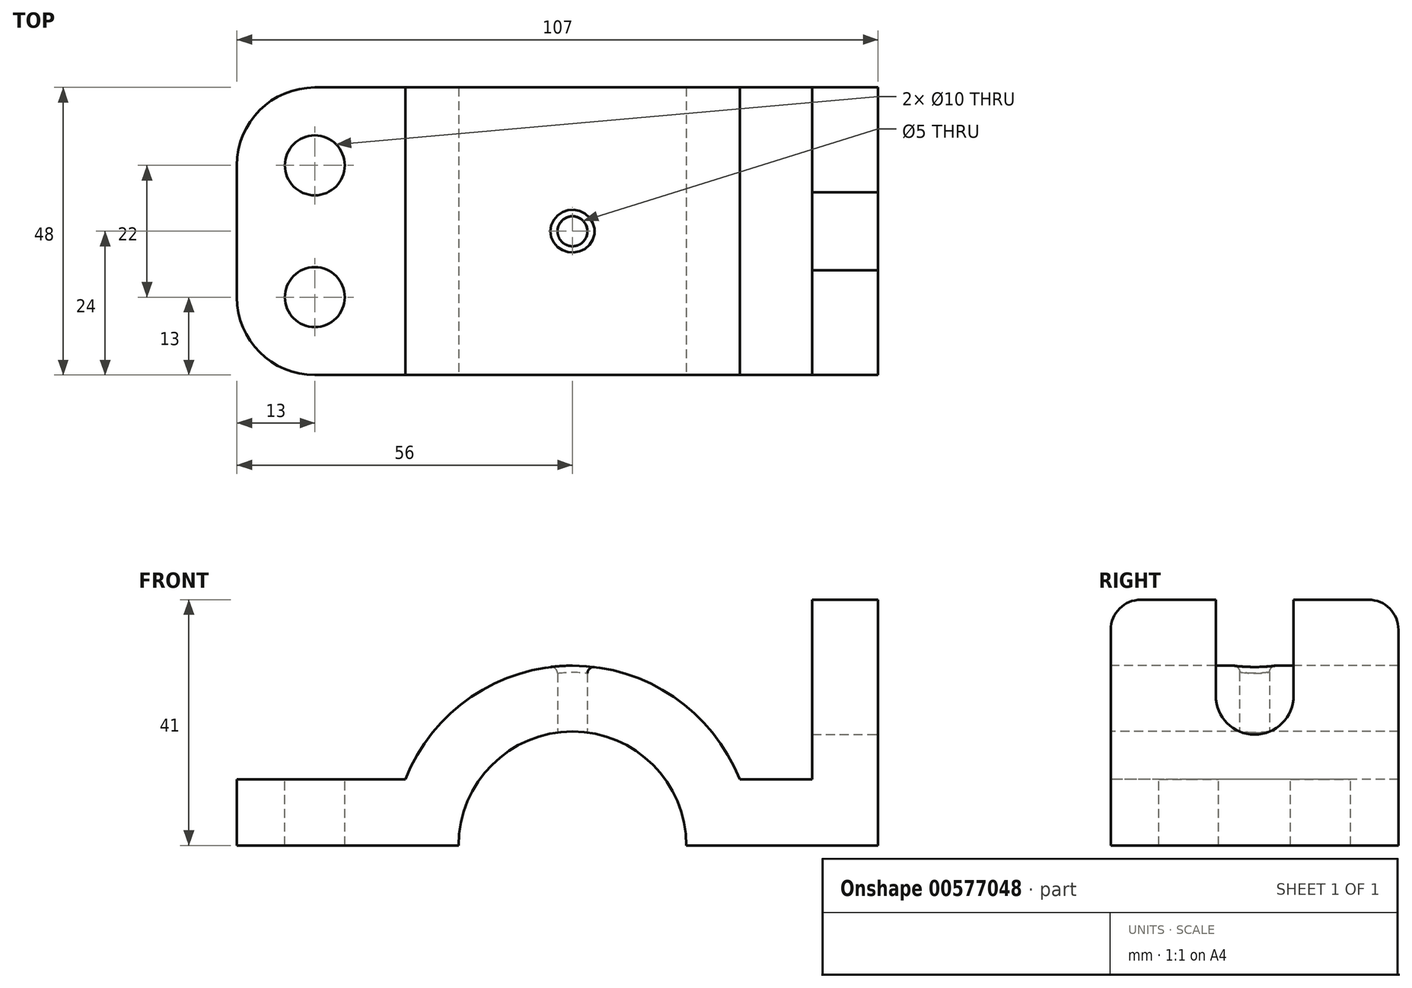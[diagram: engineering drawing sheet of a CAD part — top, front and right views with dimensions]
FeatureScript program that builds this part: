
annotation { "Feature Type Name" : "Feature", "Feature Type Description" : "" }
export const myFeature = defineFeature(function(context is Context, id is Id, definition is map)
    precondition{}
    {
        {
            var Q0;
            Q0=qCreatedBy(makeId("Front.planeOp"),FACE);
            var sketch = newSketch(context, id + "F0", { "sketchPlane" : qUnion([Q0])});
            skLineSegment(sketch, "E0", {"start": v(-56, 11) * mm, "end": v(-56, 0) * mm});
            skLineSegment(sketch, "E1", {"start": v(-56, 0) * mm, "end": v(-19, 0) * mm});
            skLineSegment(sketch, "E2", {"start": v(-56, 11) * mm, "end": v(-27.91, 11) * mm});
            skLineSegment(sketch, "E3", {"start": v(27.91, 11) * mm, "end": v(40, 11) * mm});
            skLineSegment(sketch, "E4", {"start": v(40, 11) * mm, "end": v(40, 41) * mm});
            skLineSegment(sketch, "E5", {"start": v(40, 41) * mm, "end": v(51, 41) * mm});
            skLineSegment(sketch, "E6", {"start": v(51, 41) * mm, "end": v(51, 0) * mm});
            skLineSegment(sketch, "E7", {"start": v(51, 0) * mm, "end": v(19, 0) * mm});
            skArc(sketch, "E8", {"start": v(27.91, 11) * mm, "mid": v(0, 30) * mm, "end": v(-27.91, 11) * mm});
            skArc(sketch, "E9", {"start": v(19, 0) * mm, "mid": v(0, 19) * mm, "end": v(-19, 0) * mm});
            skSolve(sketch);
        }
        {
            var Q0;
            Q0=makeQuery(id+"F0.imprint","IMPRINT",FACE,{"disambiguationData":[TD([[makeQuery(id+"F0.imprint","IMPRINT",EDGE,{"derivedFrom":sQuery(id+"F0.wireOp",EDGE,"E0")}),1.0]])]});
            extrude(context, id + "F1", {"entities" : qUnion([Q0]), "oppositeDirection" : true, "depth" : 48 * mm, "offsetDistance" : 25.4 * mm});
        }
        {
            var Q0;
            Q0=makeQuery(id+"F1.opExtrude","SWEPT_FACE",FACE,{"disambiguationData":[OSD([sQuery(id+"F0.wireOp",EDGE,"E2")])]});
            var sketch = newSketch(context, id + "F2", { "sketchPlane" : qUnion([Q0])});
            skLineSegment(sketch, "E10.0.0", {"start": v(-43, 0) * mm, "end": v(-27.91, 0) * mm});
            skLineSegment(sketch, "E10.0.1", {"start": v(-27.91, 0) * mm, "end": v(-27.91, 48) * mm});
            skLineSegment(sketch, "E10.0.2", {"start": v(-27.91, 48) * mm, "end": v(-43, 48) * mm});
            skLineSegment(sketch, "E10.0.3", {"start": v(-56, 35) * mm, "end": v(-56, 13) * mm});
            skPoint(sketch, "E11.visualSharp", {"position": v(-56, 48) * mm});
            skArc(sketch, "E11.filletArc", {"start": v(-43, 48) * mm, "mid": v(-52.2, 44.2) * mm, "end": v(-56, 35) * mm});
            skPoint(sketch, "E12.visualSharp", {"position": v(-56, 0) * mm});
            skArc(sketch, "E12.filletArc", {"start": v(-56, 13) * mm, "mid": v(-52.2, 3.8) * mm, "end": v(-43, 0) * mm});
            skCircle(sketch, "E13", {"center": v(-43, 35) * mm, "radius": 5 * mm});
            skCircle(sketch, "E14", {"center": v(-43, 13) * mm, "radius": 5 * mm});
            skSolve(sketch);
        }
        {
            var Q0;
            Q0=makeQuery(id+"F2.imprint","IMPRINT",FACE,{"disambiguationData":[TD([[makeQuery(id+"F2.imprint","IMPRINT",EDGE,{"derivedFrom":sQuery(id+"F2.wireOp",EDGE,"E13")}),1.0]])]});
            var Q1;
            Q1=makeQuery(id+"F2.imprint","IMPRINT",FACE,{"disambiguationData":[TD([[makeQuery(id+"F2.imprint","IMPRINT",EDGE,{"derivedFrom":sQuery(id+"F2.wireOp",EDGE,"E14")}),1.0]])]});
            var Q2;
            {var subQ0=sQuery(id+"F2.wireOp",EDGE,"E11.filletArc");Q2=makeQuery(id+"F2.imprint","IMPRINT",FACE,{"disambiguationData":[TD([[makeQuery(id+"F2.imprint","IMPRINT",EDGE,{"derivedFrom":subQ0}),-1.0]])]});}
            var Q3;
            {var subQ0=sQuery(id+"F2.wireOp",EDGE,"E12.filletArc");Q3=makeQuery(id+"F2.imprint","IMPRINT",FACE,{"disambiguationData":[TD([[makeQuery(id+"F2.imprint","IMPRINT",EDGE,{"derivedFrom":subQ0}),-1.0]])]});}
            var Q4;
            Q4=sQuery(id+"F2.wireOp",EDGE,"E13");
            var Q5;
            Q5=sQuery(id+"F2.wireOp",EDGE,"E14");
            extrude(context, id + "F3", {"entities" : qUnion([Q0, Q1, Q2, Q3]), "operationType" : NewBodyOperationType.REMOVE, "surfaceEntities" : qUnion([Q4, Q5]), "endBound" : BoundingType.THROUGH_ALL, "oppositeDirection" : true, "depth" : 25.4 * mm, "offsetDistance" : 25.4 * mm});
        }
        {
            var Q0;
            Q0=makeQuery(id+"F1.opExtrude","SWEPT_FACE",FACE,{"disambiguationData":[OSD([sQuery(id+"F0.wireOp",EDGE,"E6")])]});
            var sketch = newSketch(context, id + "F4", { "sketchPlane" : qUnion([Q0])});
            skLineSegment(sketch, "E15.0.0", {"start": v(0, 36) * mm, "end": v(0, 0) * mm});
            skLineSegment(sketch, "E15.0.1", {"start": v(0, 0) * mm, "end": v(48, 0) * mm});
            skLineSegment(sketch, "E15.0.2", {"start": v(48, 0) * mm, "end": v(48, 36) * mm});
            skLineSegment(sketch, "E15.0.3", {"start": v(43, 41) * mm, "end": v(30.5, 41) * mm});
            skPoint(sketch, "E16.visualSharp", {"position": v(0, 41) * mm});
            skArc(sketch, "E16.filletArc", {"start": v(5, 41) * mm, "mid": v(1.46, 39.54) * mm, "end": v(0, 36) * mm});
            skPoint(sketch, "E17.visualSharp", {"position": v(48, 41) * mm});
            skArc(sketch, "E17.filletArc", {"start": v(48, 36) * mm, "mid": v(46.54, 39.54) * mm, "end": v(43, 41) * mm});
            skLineSegment(sketch, "E18", {"start": v(17.5, 41) * mm, "end": v(17.5, 25) * mm});
            skLineSegment(sketch, "E19", {"start": v(30.5, 41) * mm, "end": v(30.5, 25) * mm});
            skArc(sketch, "E20", {"start": v(17.5, 25) * mm, "mid": v(24, 18.5) * mm, "end": v(30.5, 25) * mm});
            skLineSegment(sketch, "E21.trimOffspring", {"start": v(17.5, 41) * mm, "end": v(5, 41) * mm});
            skSolve(sketch);
        }
        {
            var Q0;
            {var subQ0=sQuery(id+"F4.wireOp",EDGE,"E18");Q0=makeQuery(id+"F4.imprint","IMPRINT",FACE,{"disambiguationData":[TD([[makeQuery(id+"F4.imprint","IMPRINT",EDGE,{"derivedFrom":subQ0}),1.0]])]});}
            extrude(context, id + "F5", {"entities" : qUnion([Q0]), "operationType" : NewBodyOperationType.REMOVE, "oppositeDirection" : true, "depth" : 15.75 * mm, "offsetDistance" : 25.4 * mm});
        }
        {
            var Q0;
            Q0=makeQuery(id+"F1.opExtrude","SWEPT_FACE",FACE,{"disambiguationData":[OSD([sQuery(id+"F0.wireOp",EDGE,"E7")])]});
            var sketch = newSketch(context, id + "F6", { "sketchPlane" : qUnion([Q0])});
            skLineSegment(sketch, "E22.0.0", {"start": v(-19, 0) * mm, "end": v(19, 0) * mm});
            skLineSegment(sketch, "E22.0.1", {"start": v(-19, 0) * mm, "end": v(-19, -48) * mm});
            skLineSegment(sketch, "E22.0.2", {"start": v(19, -48) * mm, "end": v(-19, -48) * mm});
            skLineSegment(sketch, "E22.0.3", {"start": v(19, -48) * mm, "end": v(19, 0) * mm});
            skLineSegment(sketch, "E23", {"start": v(0, 0) * mm, "end": v(0, -48) * mm, "construction": true});
            skCircle(sketch, "E24", {"center": v(0, -24) * mm, "radius": 2.5 * mm});
            skSolve(sketch);
        }
        {
            var Q0;
            Q0=makeQuery(id+"F6.imprint","IMPRINT",FACE,{"disambiguationData":[TD([[makeQuery(id+"F6.imprint","IMPRINT",EDGE,{"derivedFrom":sQuery(id+"F6.wireOp",EDGE,"E24")}),1.0]])]});
            var Q1;
            Q1=sQuery(id+"F6.wireOp",EDGE,"E24");
            extrude(context, id + "F7", {"entities" : qUnion([Q0]), "operationType" : NewBodyOperationType.REMOVE, "surfaceEntities" : qUnion([Q1]), "endBound" : BoundingType.THROUGH_ALL, "oppositeDirection" : true, "depth" : 25.4 * mm, "offsetDistance" : 25.4 * mm});
        }
        {
            var Q0;
            Q0=makeQuery(id+"F7.boolean.opBoolean","INTERSECT",EDGE,{"derivedFrom":[makeQuery(id+"F1.opExtrude","SWEPT_FACE",FACE,{"disambiguationData":[OSD([sQuery(id+"F0.wireOp",EDGE,"E8")])]}),makeQuery(id+"F7.opExtrude","SWEPT_FACE",FACE,{"disambiguationData":[OSD([sQuery(id+"F6.wireOp",EDGE,"E24")])]})]});
            fillet(context, id + "F8", {"entities" : qUnion([Q0]), "radius" : 1.06 * mm, "tangentPropagation" : true, "allowEdgeOverflow" : false});
        }
        {
            var Q0;
            Q0=makeQuery(id+"F1.opExtrude","CAP_EDGE",EDGE,{"disambiguationData":[OSD([sQuery(id+"F0.wireOp",EDGE,"E5")])],"isStart":true});
            var Q1;
            Q1=makeQuery(id+"F1.opExtrude","CAP_EDGE",EDGE,{"disambiguationData":[OSD([sQuery(id+"F0.wireOp",EDGE,"E5")])],"isStart":false});
            fillet(context, id + "F9", {"entities" : qUnion([Q0, Q1]), "radius" : 5 * mm, "tangentPropagation" : true, "allowEdgeOverflow" : false});
        }
    });
